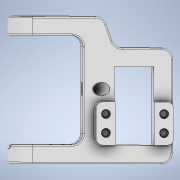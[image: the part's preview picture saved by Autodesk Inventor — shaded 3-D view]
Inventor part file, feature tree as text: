
AUTODESK INVENTOR PART (.ipt)
format: ipt  version: 2020.3 (Build 243373000, 373)  size: 546,304 bytes
history: native  units: mm
features: fillet x11, sketch x8, extrude x6, hole x5, plane x4, chamfer x1
ambient origin geometry x8: Origin, YZ Plane, XZ Plane, XY Plane, X Axis, Y Axis, Z Axis, Center Point
bodies: Solid1 (feature_tree)
feature tree (35):
  sketch  "Sketch1"  dims[d4=24.6mm d5=12.4mm]
  extrude  "Extrusion1"  Depth=12.4mm
  hole  "Hole1"  [1 undecoded]
  fillet  "Fillet1"  Radius=23.5mm
  fillet  "Fillet2"  Radius=34.5mm
  sketch  "Sketch2"  dims[d9=6.0mm d11=10.0mm d12=23.5mm d14=34.5mm]
  hole  "Hole2"  [1 undecoded]
  sketch  "Sketch8"  dims[d19=1.9mm d20=6.0mm d21=4.0mm d22=2.0mm d23=90.0deg d24=10.0mm d25=20.594885mm]
  extrude  "Extrusion3"  Depth=6.0mm
  extrude  "Extrusion4"  Depth=3.7mm
  hole  "Hole5"  [1 undecoded]
  fillet  "Fillet4"  Radius=10.0mm
  fillet  "Fillet9"  Radius=3.5mm
  fillet  "Fillet10"  Radius=0.5mm
  fillet  "Fillet5"  Radius=0.5mm
  fillet  "Fillet6"  Radius=28.4mm
  hole  "Hole4"  [1 undecoded]
  fillet  "Fillet11"  Radius=6.0mm
  extrude  "Extrusion6"  Depth=2.0mm
  plane  "Work Plane1"
  extrude  "Extrusion7"  Depth=0.5mm
  fillet  "Fillet12"  Radius=2.0mm
  hole  "Hole6"  [1 undecoded]
  plane  "Work Plane3"
  extrude  "Extrusion8"  Depth=2.0mm
  chamfer  "Chamfer1"  Distance=0.3mm
  fillet  "Fillet13"  Radius=0.2mm
  fillet  "Fillet14"  [1 undecoded]
  plane  "Work Plane5"
  plane  "Work Plane6"
  sketch  "Sketch3"  dims[d16=6.0mm d17=15.0mm d18=0.0mm]
  sketch  "Sketch9"  dims[d27=8.8mm d28=6.0mm d29=4.0mm d30=2.0mm d31=90.0deg d32=8.0mm d33=20.594885mm d34=6.0mm]
  sketch  "Sketch10"  dims[d37=7.2mm d38=3.7mm]
  sketch  "Sketch11"  dims[d39=12.1mm d40=3.5mm d41=0.0mm d42=10.0mm d43=0.0mm d53=3.5mm d54=0.5mm d55=0.5mm d57=28.4mm]
  sketch  "Sketch12"  dims[d58=6.8mm d59=20.92mm d60=0.0mm d61=6.0mm d62=3.0mm d63=6.0mm d64=4.0mm d65=2.0mm d66=90.0deg d67=4.3mm d68=0.0mm d70=2.0mm d71=0.5mm d72=2.0mm d74=2.0mm d75=2.0mm d76=1.0mm d77=6.0mm d78=4.0mm d79=2.0mm d80=90.0deg d81=8.0mm d82=20.594885mm d83=0.3mm d84=0.2mm d85=0.0mm d86=0.0mm d87=1.0mm d88=3.5mm d89=-9.075712mm d90=4.0mm d91=4.0mm d92=1.0mm d93=33.941mm d94=0.0mm d95=0.2mm d96=2.1mm d97=6.0mm d98=4.0mm d99=2.0mm d100=90.0deg d101=7.3mm d102=0.0mm d103=24.0mm d104=7.0mm d105=7.0mm d106=0.0mm d107=0.2mm d108=0.8mm d109=45.0deg d110=1.0mm d111=2.0mm d112=3.490659mm d113=16.0mm d114=-7.5mm]
note: 6 required parameter values undecoded (feature->parameter linkage not recoverable at this tier; creation-order binding heuristic only, values carry confidence <= 0.55)
